# Revit family: GRIBLO LED SMD
name_source: partatom
category: Lighting Fixtures
revit_build: Autodesk Revit Architecture 2015 (Build: 20140322_1515(x64)
units: mm (PartAtom-declared; Revit-internal decimal feet)

## types (1)
- GRIBLO LED SMD-NW 18131 LED 4500K 35° 170lm aluminium szary
    Apparent Load = 4 VA
    Default Elevation = 0 mm  [stored 0 ft]
    IP = IP65
    Klasyfikacja obciążenia = Oświetlenie
    Kod = 18131
    Kąt rozsyłu = 35°
    Lamp = LED
    Manufacturer = KANLUX
    Materiał klosz = KANLUX - szkło
    Materiał obudowa = KANLUX - obudowa - aluminium, szary
    Materiał obudowa część = KANLUX - obudowa - tworzwo sztuczne
    Moc oprawy = 4 W
    Model = GRIBLO LED SMD-NW
    Strumień świetlny = 170 lm
    Szerokość = 62 mm
    Temperatura barwowa = 4500 K
    URL = www.kanlux.pl
    Wattage Comments = 4
    Współczynnik mocy = 1
    Wysokość = 263 mm
    Średnica = 65 mm

note: [stored X ft] marks values corroborated as IEEE doubles in the binary element streams (Revit-internal decimal feet)

## geometry (parser evidence)
native form markers: Sweep x3
no freeform markers — native parametric forms only
